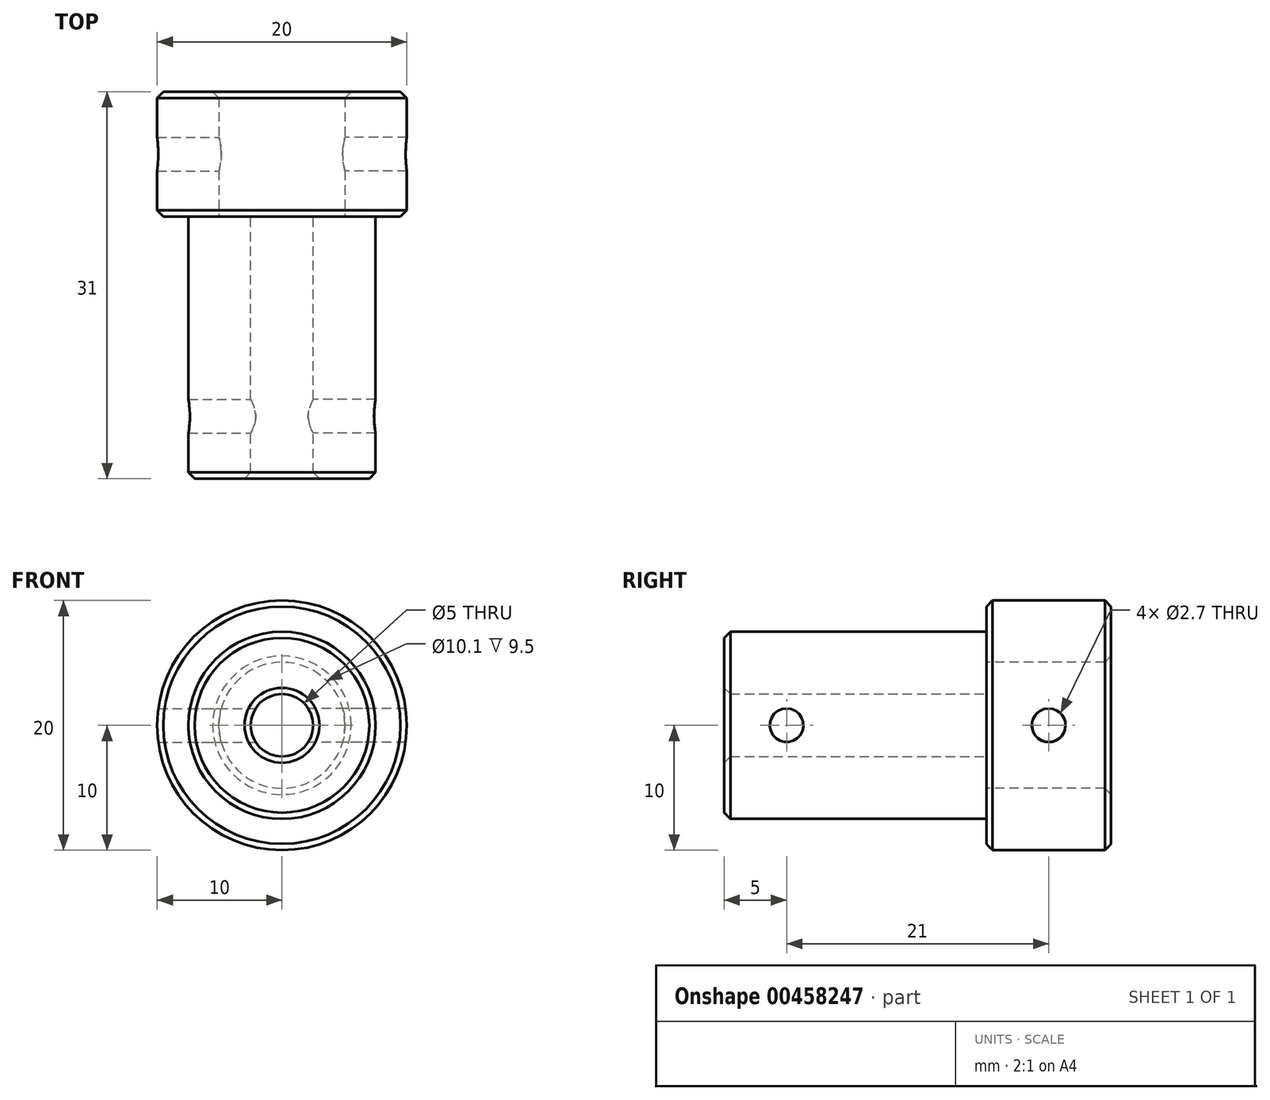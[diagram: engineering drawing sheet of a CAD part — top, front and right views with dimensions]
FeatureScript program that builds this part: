
annotation { "Feature Type Name" : "Feature", "Feature Type Description" : "" }
export const myFeature = defineFeature(function(context is Context, id is Id, definition is map)
    precondition{}
    {
        {
            var Q0;
            Q0=qCreatedBy(makeId("Front.planeOp"),FACE);
            var sketch = newSketch(context, id + "F0", { "sketchPlane" : qUnion([Q0])});
            skCircle(sketch, "E0", {"center": v(0, 0) * mm, "radius": 2.5 * mm});
            skCircle(sketch, "E1", {"center": v(0, 0) * mm, "radius": 7.5 * mm});
            skSolve(sketch);
        }
        {
            var Q0;
            Q0 = qSketchRegion(id + "F0", true);
            extrude(context, id + "F1", {"entities" : qUnion([Q0]), "depth" : 21 * mm, "offsetDistance" : 25 * mm});
        }
        {
            var Q0;
            Q0=qCreatedBy(makeId("Front.planeOp"),FACE);
            var sketch = newSketch(context, id + "F2", { "sketchPlane" : qUnion([Q0])});
            skCircle(sketch, "E2", {"center": v(0, 0) * mm, "radius": 5.05 * mm});
            skCircle(sketch, "E3", {"center": v(0, 0) * mm, "radius": 10 * mm});
            skSolve(sketch);
        }
        {
            var Q0;
            Q0 = qSketchRegion(id + "F2", true);
            extrude(context, id + "F3", {"entities" : qUnion([Q0]), "operationType" : NewBodyOperationType.ADD, "oppositeDirection" : true, "depth" : 10 * mm});
        }
        {
            var Q0;
            Q0=qCreatedBy(makeId("Right.planeOp"),FACE);
            var sketch = newSketch(context, id + "F4", { "sketchPlane" : qUnion([Q0])});
            skPoint(sketch, "E4", {"position": v(5, 0) * mm});
            skPoint(sketch, "E5", {"position": v(-16, 0) * mm});
            skSolve(sketch);
        }
        {
            var Q0;
            Q0=sQuery(id+"F4.wireOp",VERTEX,"E4");
            var Q1;
            Q1=sQuery(id+"F4.wireOp",VERTEX,"E5");
            var Q2;
            Q2=makeQuery(id+"F3.opExtrude","SWEPT_BODY",BODY,{"disambiguationData":[OSD([sQuery(id+"F2.wireOp",EDGE,"E2"),sQuery(id+"F2.wireOp",EDGE,"E3")])]});
            var Q3;
            Q3=makeQuery(id+"F1.opExtrude","SWEPT_BODY",BODY,{"disambiguationData":[OSD([sQuery(id+"F0.wireOp",EDGE,"E0"),sQuery(id+"F0.wireOp",EDGE,"E1")])]});
            hole(context, id + "F5", {"style" : HoleStyle.SIMPLE, "endStyle" : HoleEndStyle.THROUGH, "standardTappedOrClearance" : lookupTablePath({ "standard" : "ISO", "engagement" : "50%", "pitch" : "0.5 mm", "size" : "M3", "type" : "Tapped" }), "standardBlindInLast" : lookupTablePath({ "standard" : "ISO", "engagement" : "50%", "pitch" : "0.5 mm", "size" : "M3", "type" : "Tapped" }), "holeDiameter" : 2.7 * mm, "showTappedDepth" : true, "isTappedThrough" : true, "tappedDepth" : 12 * mm, "tapClearance" : 3, "locations" : qUnion([Q0, Q1]), "scope" : qUnion([Q2, Q3]), "majorDiameter" : 3 * mm});
        }
        {
            var Q0;
            Q0=makeQuery(id+"F3.opExtrude","CAP_EDGE",EDGE,{"disambiguationData":[OSD([sQuery(id+"F2.wireOp",EDGE,"E3")])],"isStart":false});
            var Q1;
            Q1=makeQuery(id+"F3.opExtrude","CAP_EDGE",EDGE,{"disambiguationData":[OSD([sQuery(id+"F2.wireOp",EDGE,"E2")])],"isStart":false});
            var Q2;
            Q2=makeQuery(id+"F3.opExtrude","CAP_EDGE",EDGE,{"disambiguationData":[OSD([sQuery(id+"F2.wireOp",EDGE,"E3")])],"isStart":true});
            var Q3;
            Q3=makeQuery(id+"F1.opExtrude","CAP_EDGE",EDGE,{"disambiguationData":[OSD([sQuery(id+"F0.wireOp",EDGE,"E1")])],"isStart":false});
            var Q4;
            Q4=makeQuery(id+"F1.opExtrude","CAP_EDGE",EDGE,{"disambiguationData":[OSD([sQuery(id+"F0.wireOp",EDGE,"E0")])],"isStart":false});
            chamfer(context, id + "F6", {"entities" : qUnion([Q0, Q1, Q2, Q3, Q4]), "width" : 0.5 * mm, "tangentPropagation" : true});
        }
        {
            var Q0;
            Q0=sQuery(id+"F4.wireOp",VERTEX,"E4");
            var Q1;
            Q1=sQuery(id+"F4.wireOp",VERTEX,"E5");
            var Q2;
            Q2=makeQuery(id+"F1.opExtrude","SWEPT_BODY",BODY,{"disambiguationData":[OSD([sQuery(id+"F0.wireOp",EDGE,"E0"),sQuery(id+"F0.wireOp",EDGE,"E1")])]});
            hole(context, id + "F7", {"style" : HoleStyle.SIMPLE, "endStyle" : HoleEndStyle.THROUGH, "oppositeDirection" : true, "standardTappedOrClearance" : lookupTablePath({ "standard" : "ISO", "engagement" : "50%", "pitch" : "0.5 mm", "size" : "M3", "type" : "Tapped" }), "standardBlindInLast" : lookupTablePath({ "standard" : "ISO", "engagement" : "50%", "pitch" : "0.5 mm", "size" : "M3", "type" : "Tapped" }), "holeDiameter" : 2.7 * mm, "showTappedDepth" : true, "isTappedThrough" : true, "tappedDepth" : 12 * mm, "tapClearance" : 3, "locations" : qUnion([Q0, Q1]), "scope" : qUnion([Q2]), "majorDiameter" : 3 * mm});
        }
    });
